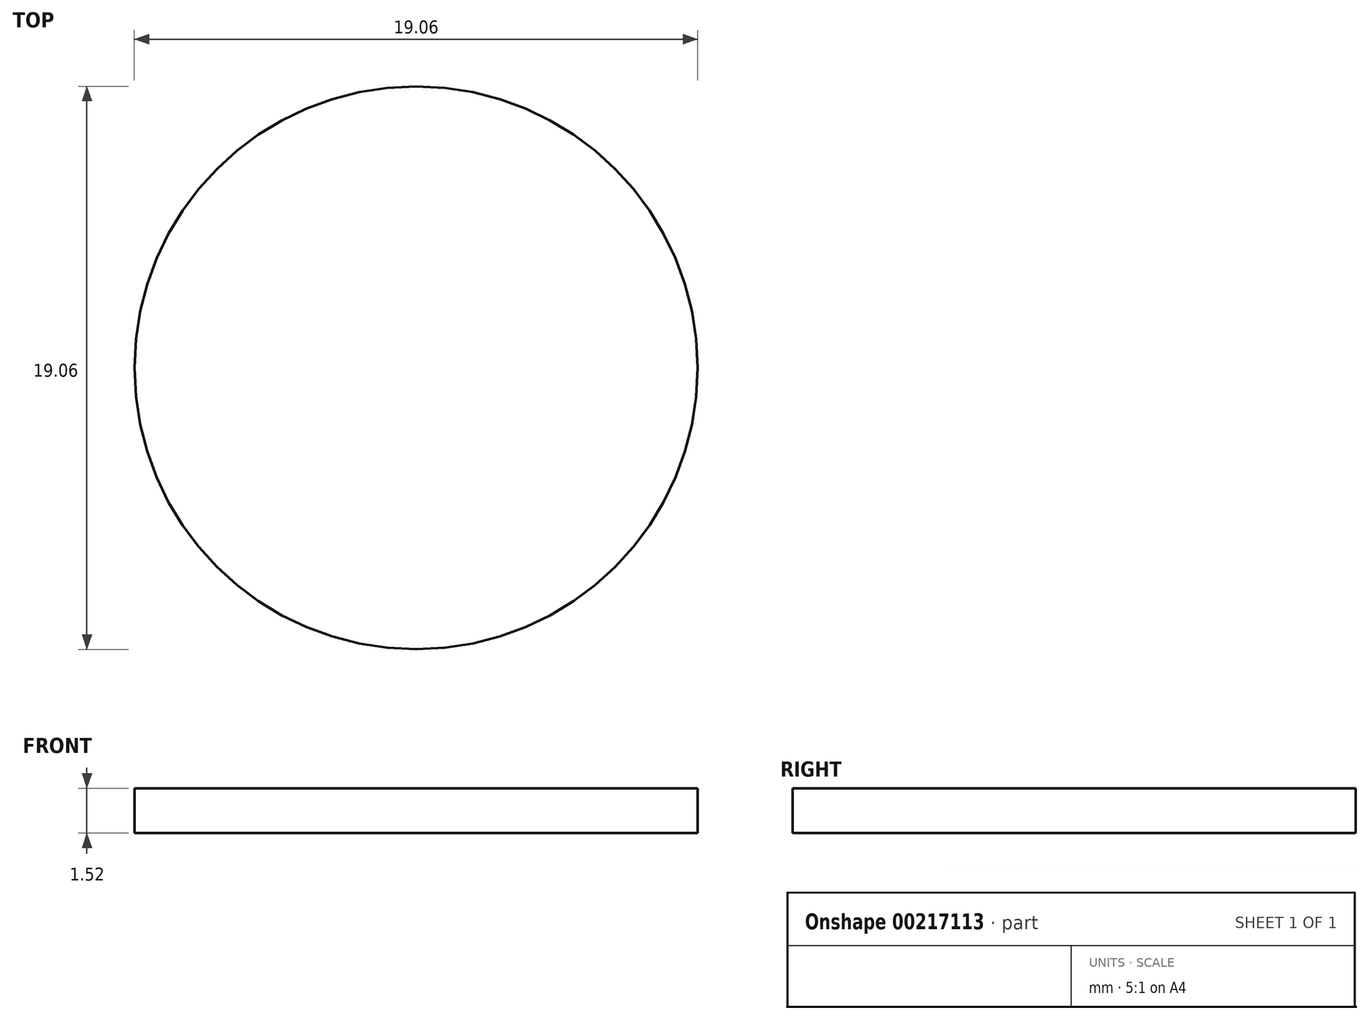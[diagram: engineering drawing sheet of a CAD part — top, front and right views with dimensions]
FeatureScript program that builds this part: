
annotation { "Feature Type Name" : "Feature", "Feature Type Description" : "" }
export const myFeature = defineFeature(function(context is Context, id is Id, definition is map)
    precondition{}
    {
        {
            var Q0;
            Q0=qCreatedBy(makeId("Top.planeOp"),FACE);
            var sketch = newSketch(context, id + "F0", { "sketchPlane" : qUnion([Q0])});
            skCircle(sketch, "E0", {"center": v(0, 0) * mm, "radius": 9.53 * mm});
            skSolve(sketch);
        }
        {
            var Q0;
            Q0 = qSketchRegion(id + "F0", true);
            extrude(context, id + "F1", {"entities" : qUnion([Q0]), "endBound" : BoundingType.SYMMETRIC, "depth" : 1.52 * mm});
        }
    });
